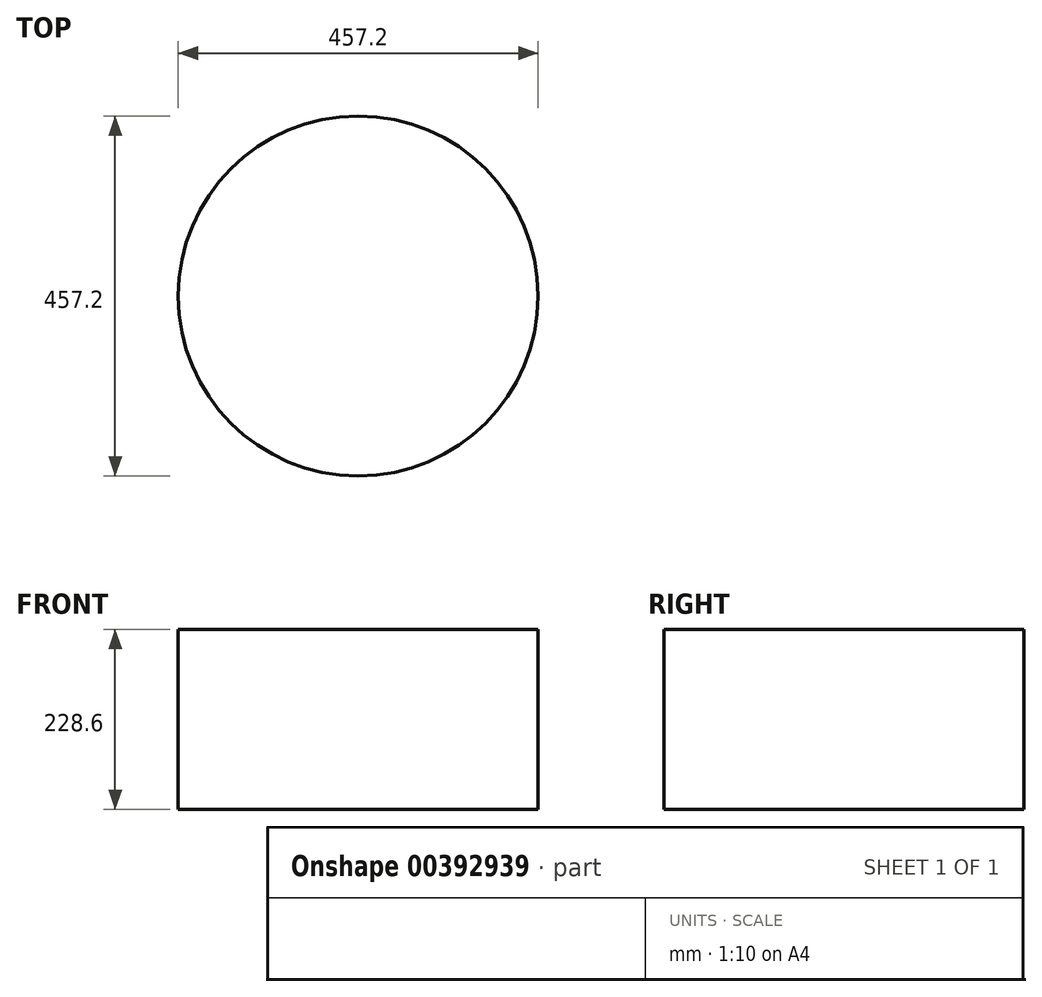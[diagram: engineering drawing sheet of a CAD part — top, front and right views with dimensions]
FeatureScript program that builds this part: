
annotation { "Feature Type Name" : "Feature", "Feature Type Description" : "" }
export const myFeature = defineFeature(function(context is Context, id is Id, definition is map)
    precondition{}
    {
        {
            var Q0;
            Q0=qCreatedBy(makeId("Top.planeOp"),FACE);
            var sketch = newSketch(context, id + "F0", { "sketchPlane" : qUnion([Q0])});
            skCircle(sketch, "E0", {"center": v(0, 0) * mm, "radius": 228.6 * mm});
            skSolve(sketch);
        }
        {
            var Q0;
            Q0 = qSketchRegion(id + "F0", true);
            extrude(context, id + "F1", {"entities" : qUnion([Q0]), "depth" : 228.6 * mm});
        }
    });
